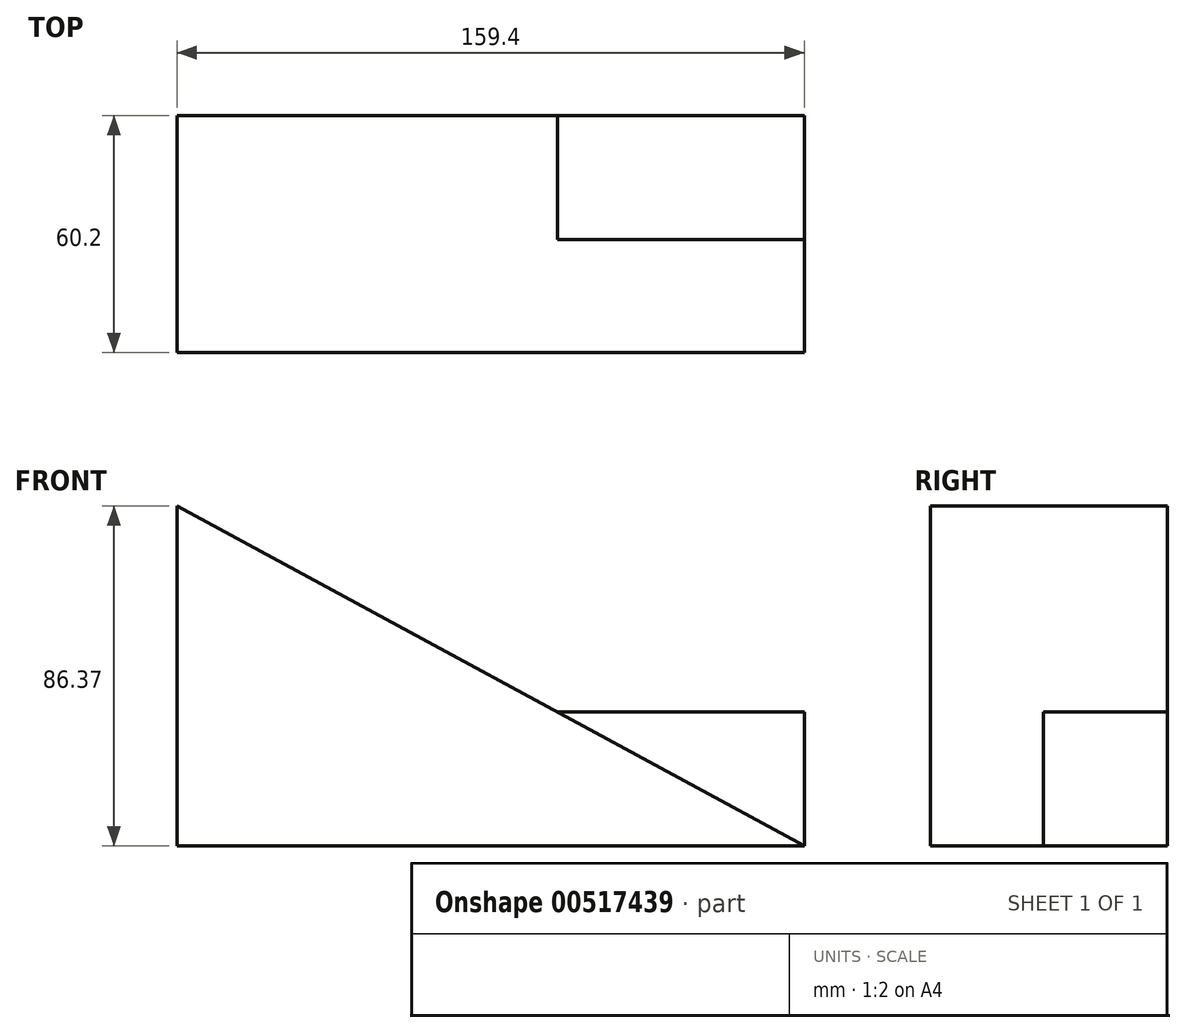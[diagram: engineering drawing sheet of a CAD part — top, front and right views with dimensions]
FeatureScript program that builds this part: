
annotation { "Feature Type Name" : "Feature", "Feature Type Description" : "" }
export const myFeature = defineFeature(function(context is Context, id is Id, definition is map)
    precondition{}
    {
        {
            var Q0;
            Q0=qCreatedBy(makeId("Front.planeOp"),FACE);
            var sketch = newSketch(context, id + "F0", { "sketchPlane" : qUnion([Q0])});
            skLineSegment(sketch, "E0", {"start": v(-83.51, 42.55) * mm, "end": v(-83.51, -43.82) * mm});
            skLineSegment(sketch, "E1", {"start": v(-83.51, -43.82) * mm, "end": v(75.9, -43.82) * mm});
            skLineSegment(sketch, "E2", {"start": v(75.9, -43.82) * mm, "end": v(-83.51, 42.55) * mm});
            skSolve(sketch);
        }
        {
            var Q0;
            Q0 = qSketchRegion(id + "F0", true);
            extrude(context, id + "F1", {"entities" : qUnion([Q0]), "depth" : 60.2 * mm, "offsetDistance" : 25.4 * mm});
        }
        {
            var Q0;
            Q0=makeQuery(id+"F1.opExtrude","CAP_FACE",FACE,{"disambiguationData":[OSD([sQuery(id+"F0.wireOp",EDGE,"E0"),sQuery(id+"F0.wireOp",EDGE,"E1"),sQuery(id+"F0.wireOp",EDGE,"E2")])],"isStart":true});
            var sketch = newSketch(context, id + "F2", { "sketchPlane" : qUnion([Q0])});
            skLineSegment(sketch, "E3", {"start": v(-75.9, -43.82) * mm, "end": v(-75.9, -9.82) * mm});
            skLineSegment(sketch, "E4", {"start": v(-75.9, -9.82) * mm, "end": v(-13.14, -9.82) * mm});
            skSolve(sketch);
        }
        {
            var Q0;
            {var subQ0=sQuery(id+"F2.wireOp",EDGE,"E3");Q0=makeQuery(id+"F2.imprint","IMPRINT",FACE,{"disambiguationData":[TD([[makeQuery(id+"F2.imprint","IMPRINT",EDGE,{"derivedFrom":subQ0}),-1.0]])]});}
            extrude(context, id + "F3", {"entities" : qUnion([Q0]), "operationType" : NewBodyOperationType.ADD, "oppositeDirection" : true, "depth" : 31.5 * mm, "offsetDistance" : 25.4 * mm});
        }
    });
